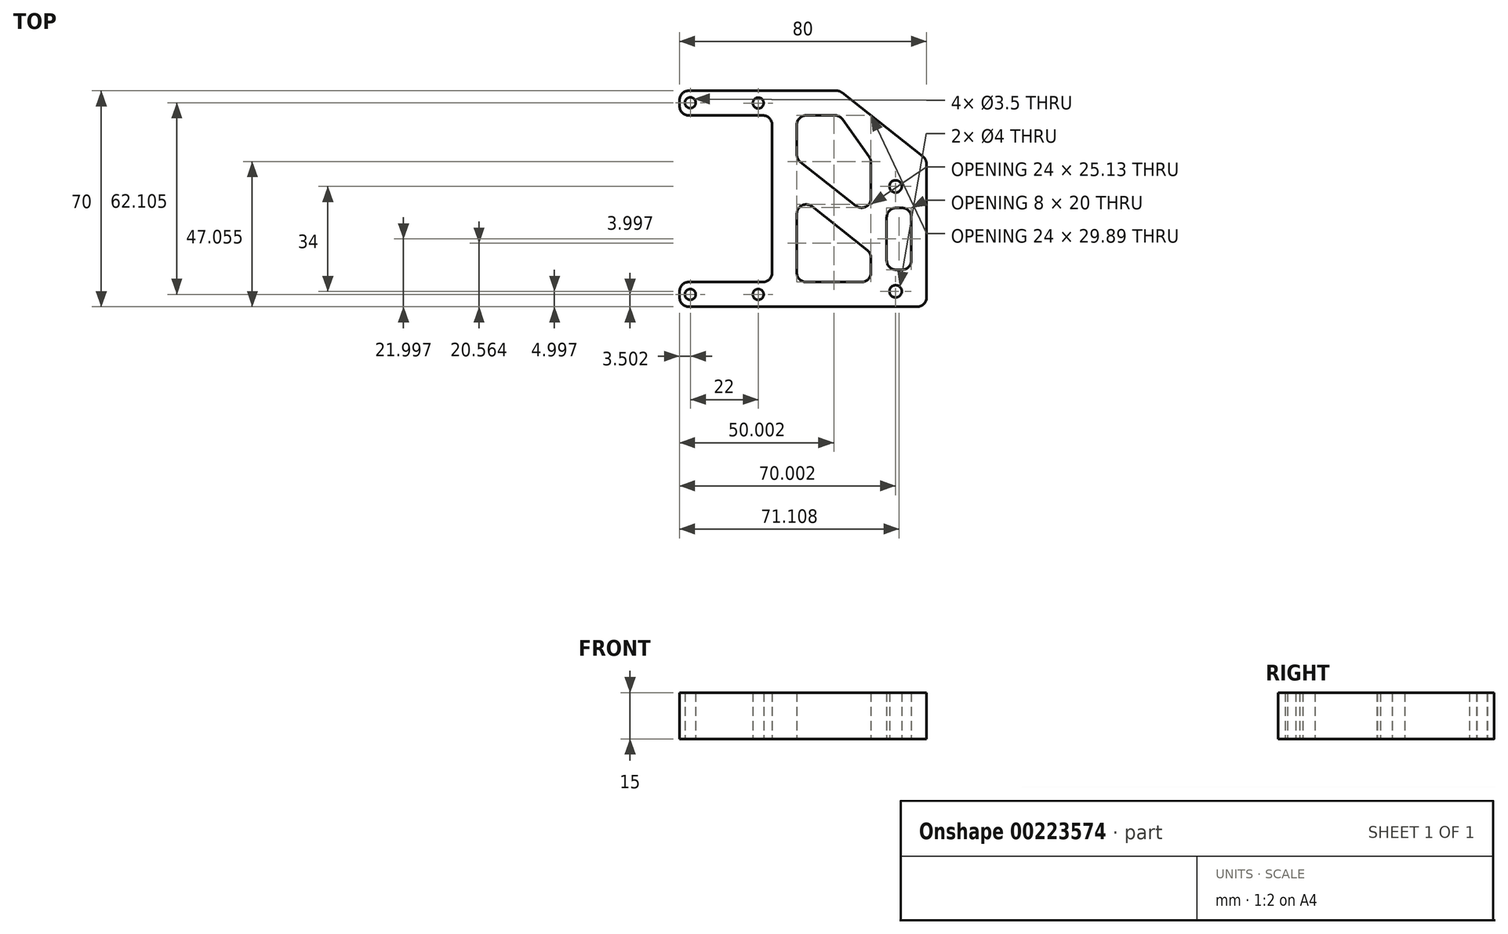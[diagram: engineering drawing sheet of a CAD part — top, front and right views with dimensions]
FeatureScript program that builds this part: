
annotation { "Feature Type Name" : "Feature", "Feature Type Description" : "" }
export const myFeature = defineFeature(function(context is Context, id is Id, definition is map)
    precondition{}
    {
        {
            var Q0;
            Q0=qCreatedBy(makeId("Top.planeOp"),FACE);
            var sketch = newSketch(context, id + "F0", { "sketchPlane" : qUnion([Q0])});
            skCircle(sketch, "E0", {"center": v(21.8, -30.22) * mm, "radius": 2 * mm});
            skCircle(sketch, "E1", {"center": v(21.8, 3.78) * mm, "radius": 2 * mm});
            skLineSegment(sketch, "E2.bottom", {"start": v(2.61, 34.78) * mm, "end": v(-45.2, 34.78) * mm});
            skLineSegment(sketch, "E2.top", {"start": v(28.8, -35.22) * mm, "end": v(-45.2, -35.22) * mm});
            skLineSegment(sketch, "E2.left", {"start": v(31.8, 11.09) * mm, "end": v(31.8, -32.22) * mm});
            skLineSegment(sketch, "E2.right", {"start": v(-48.2, 31.78) * mm, "end": v(-48.2, 29.78) * mm});
            skPoint(sketch, "E3.visualSharp", {"position": v(31.8, 34.78) * mm});
            skLineSegment(sketch, "E4", {"start": v(-45.2, -27.22) * mm, "end": v(-21.2, -27.22) * mm});
            skLineSegment(sketch, "E5", {"start": v(-18.2, -24.22) * mm, "end": v(-18.2, 23.78) * mm});
            skLineSegment(sketch, "E6", {"start": v(-21.2, 26.78) * mm, "end": v(-45.2, 26.78) * mm});
            skLineSegment(sketch, "E7.trimOffspring", {"start": v(-48.2, -30.22) * mm, "end": v(-48.2, -32.22) * mm});
            skLineSegment(sketch, "E8", {"start": v(4.47, 34.13) * mm, "end": v(30.65, 13.44) * mm});
            skPoint(sketch, "E9.visualSharp", {"position": v(-18.2, 26.78) * mm});
            skArc(sketch, "E9.filletArc", {"start": v(-18.2, 23.78) * mm, "mid": v(-19.09, 25.9) * mm, "end": v(-21.2, 26.78) * mm});
            skPoint(sketch, "E10.visualSharp", {"position": v(-18.2, -27.22) * mm});
            skArc(sketch, "E10.filletArc", {"start": v(-21.2, -27.22) * mm, "mid": v(-19.09, -26.34) * mm, "end": v(-18.2, -24.22) * mm});
            skPoint(sketch, "E11.visualSharp", {"position": v(-48.2, -35.22) * mm});
            skArc(sketch, "E11.filletArc", {"start": v(-48.2, -32.22) * mm, "mid": v(-47.33, -34.34) * mm, "end": v(-45.2, -35.22) * mm});
            skPoint(sketch, "E12.visualSharp", {"position": v(-48.2, -27.22) * mm});
            skArc(sketch, "E12.filletArc", {"start": v(-45.2, -27.22) * mm, "mid": v(-47.33, -28.1) * mm, "end": v(-48.2, -30.22) * mm});
            skPoint(sketch, "E13.visualSharp", {"position": v(-48.2, 34.78) * mm});
            skArc(sketch, "E13.filletArc", {"start": v(-45.2, 34.78) * mm, "mid": v(-47.33, 33.9) * mm, "end": v(-48.2, 31.78) * mm});
            skPoint(sketch, "E14.visualSharp", {"position": v(-48.2, 26.78) * mm});
            skArc(sketch, "E14.filletArc", {"start": v(-48.2, 29.78) * mm, "mid": v(-47.33, 27.66) * mm, "end": v(-45.2, 26.78) * mm});
            skPoint(sketch, "E15.visualSharp", {"position": v(3.65, 34.78) * mm});
            skArc(sketch, "E15.filletArc", {"start": v(4.47, 34.13) * mm, "mid": v(3.6, 34.61) * mm, "end": v(2.61, 34.78) * mm});
            skPoint(sketch, "E16.visualSharp", {"position": v(31.8, 12.54) * mm});
            skArc(sketch, "E16.filletArc", {"start": v(31.8, 11.09) * mm, "mid": v(31.5, 12.4) * mm, "end": v(30.65, 13.44) * mm});
            skPoint(sketch, "E17.visualSharp", {"position": v(31.8, -35.22) * mm});
            skArc(sketch, "E17.filletArc", {"start": v(28.8, -35.22) * mm, "mid": v(30.91, -34.34) * mm, "end": v(31.8, -32.22) * mm});
            skLineSegment(sketch, "E18.bottom", {"start": v(-7.2, 26.78) * mm, "end": v(2.1, 26.78) * mm});
            skLineSegment(sketch, "E18.top", {"start": v(-7.2, -27.22) * mm, "end": v(10.8, -27.22) * mm});
            skLineSegment(sketch, "E18.left", {"start": v(-10.2, 23.78) * mm, "end": v(-10.2, 14.1) * mm});
            skLineSegment(sketch, "E18.right", {"start": v(13.8, 26.78) * mm, "end": v(13.8, 26.77) * mm});
            skLineSegment(sketch, "E19", {"start": v(4.55, 25.52) * mm, "end": v(13.24, 13.32) * mm});
            skLineSegment(sketch, "E20.trimOffspring", {"start": v(13.78, 26.78) * mm, "end": v(13.8, 26.78) * mm});
            skLineSegment(sketch, "E21.trimOffspring", {"start": v(13.8, 11.58) * mm, "end": v(13.8, -0.13) * mm});
            skPoint(sketch, "E22.visualSharp", {"position": v(-10.2, 26.78) * mm});
            skArc(sketch, "E22.filletArc", {"start": v(-7.2, 26.78) * mm, "mid": v(-9.33, 25.9) * mm, "end": v(-10.2, 23.78) * mm});
            skPoint(sketch, "E23.visualSharp", {"position": v(-10.2, -27.22) * mm});
            skArc(sketch, "E23.filletArc", {"start": v(-10.2, -24.22) * mm, "mid": v(-9.33, -26.34) * mm, "end": v(-7.2, -27.22) * mm});
            skPoint(sketch, "E24.visualSharp", {"position": v(13.8, -27.22) * mm});
            skArc(sketch, "E24.filletArc", {"start": v(10.8, -27.22) * mm, "mid": v(12.91, -26.34) * mm, "end": v(13.8, -24.22) * mm});
            skPoint(sketch, "E25.visualSharp", {"position": v(13.8, 12.54) * mm});
            skArc(sketch, "E25.filletArc", {"start": v(13.8, 11.58) * mm, "mid": v(13.65, 12.5) * mm, "end": v(13.24, 13.32) * mm});
            skPoint(sketch, "E26.visualSharp", {"position": v(3.65, 26.78) * mm});
            skArc(sketch, "E26.filletArc", {"start": v(4.55, 25.52) * mm, "mid": v(3.48, 26.44) * mm, "end": v(2.1, 26.78) * mm});
            skLineSegment(sketch, "E27", {"start": v(12.65, -16.94) * mm, "end": v(-5.35, -2.72) * mm});
            skLineSegment(sketch, "E28", {"start": v(8.93, -2.48) * mm, "end": v(-9.07, 11.74) * mm});
            skLineSegment(sketch, "E29.trimOffspring", {"start": v(-10.2, -5.07) * mm, "end": v(-10.2, -24.22) * mm});
            skLineSegment(sketch, "E30.trimOffspring", {"start": v(13.8, -19.3) * mm, "end": v(13.8, -24.22) * mm});
            skPoint(sketch, "E31.visualSharp", {"position": v(-10.2, 1.12) * mm});
            skArc(sketch, "E31.filletArc", {"start": v(-5.35, -2.72) * mm, "mid": v(-8.52, -2.37) * mm, "end": v(-10.2, -5.07) * mm});
            skPoint(sketch, "E32.visualSharp", {"position": v(-10.2, 12.64) * mm});
            skArc(sketch, "E32.filletArc", {"start": v(-10.2, 14.1) * mm, "mid": v(-9.9, 12.79) * mm, "end": v(-9.07, 11.74) * mm});
            skPoint(sketch, "E33.visualSharp", {"position": v(13.8, -6.32) * mm});
            skArc(sketch, "E33.filletArc", {"start": v(8.93, -2.48) * mm, "mid": v(12.1, -2.83) * mm, "end": v(13.8, -0.13) * mm});
            skPoint(sketch, "E34.visualSharp", {"position": v(13.8, -17.84) * mm});
            skArc(sketch, "E34.filletArc", {"start": v(13.8, -19.3) * mm, "mid": v(13.5, -17.99) * mm, "end": v(12.65, -16.94) * mm});
            skCircle(sketch, "E35", {"center": v(-22.7, 30.78) * mm, "radius": 1.75 * mm});
            skCircle(sketch, "E36", {"center": v(-44.7, 30.88) * mm, "radius": 1.75 * mm});
            skLineSegment(sketch, "E37.bottom", {"start": v(21.9, -3.22) * mm, "end": v(23.9, -3.22) * mm});
            skLineSegment(sketch, "E37.top", {"start": v(21.9, -23.22) * mm, "end": v(23.9, -23.22) * mm});
            skLineSegment(sketch, "E37.left", {"start": v(18.9, -6.22) * mm, "end": v(18.9, -20.22) * mm});
            skLineSegment(sketch, "E37.right", {"start": v(26.9, -6.22) * mm, "end": v(26.9, -20.22) * mm});
            skPoint(sketch, "E38.visualSharp", {"position": v(18.9, -3.22) * mm});
            skArc(sketch, "E38.filletArc", {"start": v(21.9, -3.22) * mm, "mid": v(19.78, -4.1) * mm, "end": v(18.9, -6.22) * mm});
            skPoint(sketch, "E39.visualSharp", {"position": v(18.9, -23.22) * mm});
            skArc(sketch, "E39.filletArc", {"start": v(18.9, -20.22) * mm, "mid": v(19.78, -22.34) * mm, "end": v(21.9, -23.22) * mm});
            skPoint(sketch, "E40.visualSharp", {"position": v(26.9, -23.22) * mm});
            skArc(sketch, "E40.filletArc", {"start": v(23.9, -23.22) * mm, "mid": v(26.02, -22.34) * mm, "end": v(26.9, -20.22) * mm});
            skPoint(sketch, "E41.visualSharp", {"position": v(26.9, -3.22) * mm});
            skArc(sketch, "E41.filletArc", {"start": v(26.9, -6.22) * mm, "mid": v(26.02, -4.1) * mm, "end": v(23.9, -3.22) * mm});
            skCircle(sketch, "E42", {"center": v(-44.7, -31.22) * mm, "radius": 1.75 * mm});
            skCircle(sketch, "E43", {"center": v(-22.7, -31.22) * mm, "radius": 1.75 * mm});
            skSolve(sketch);
        }
        {
            var Q0;
            Q0=makeQuery(id+"F0.imprint","IMPRINT",FACE,{"disambiguationData":[TD([[makeQuery(id+"F0.imprint","IMPRINT",EDGE,{"derivedFrom":sQuery(id+"F0.wireOp",EDGE,"E0")}),-1.0]])]});
            extrude(context, id + "F1", {"entities" : qUnion([Q0]), "depth" : 15 * mm});
        }
    });
